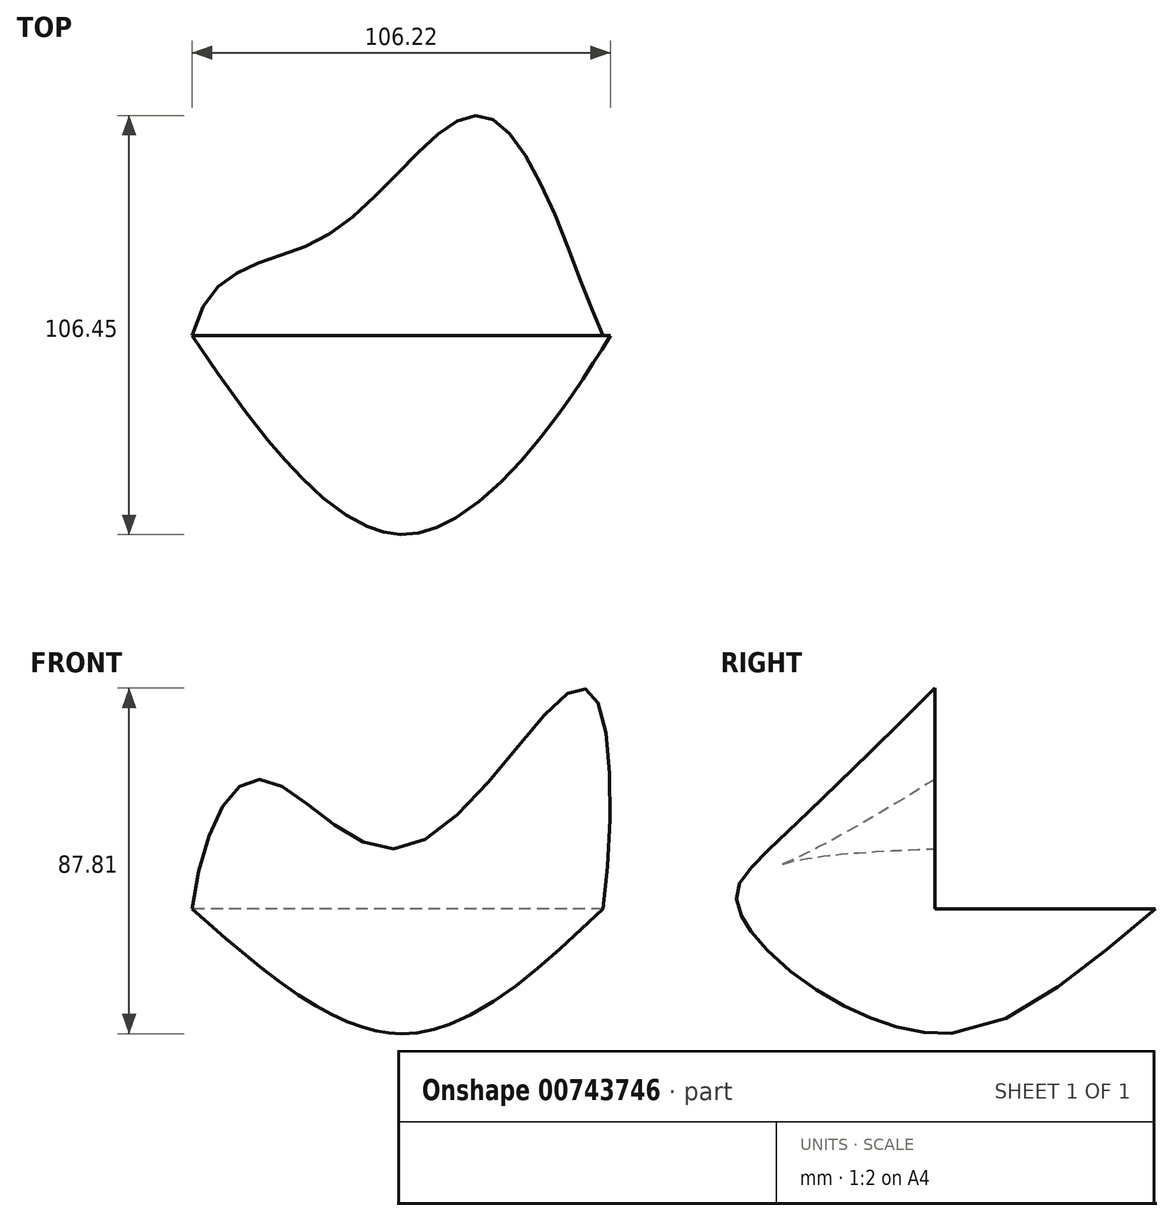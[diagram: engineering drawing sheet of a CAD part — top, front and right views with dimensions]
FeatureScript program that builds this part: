
annotation { "Feature Type Name" : "Feature", "Feature Type Description" : "" }
export const myFeature = defineFeature(function(context is Context, id is Id, definition is map)
    precondition{}
    {
        {
            var Q0;
            Q0=qCreatedBy(makeId("Top.planeOp"),FACE);
            var sketch = newSketch(context, id + "F0", { "sketchPlane" : qUnion([Q0])});
            skFitSpline(sketch, "E0", {"points": [v(-53.72, 0) * mm, v(0, -49.94) * mm, v(50.68, 0) * mm], "startDerivative": vector(107.77, -149.45) * mm, "endDerivative": vector(101.01, 150.21) * mm});
            skSolve(sketch);
        }
        {
            var Q0;
            Q0=qCreatedBy(makeId("Front.planeOp"),FACE);
            var sketch = newSketch(context, id + "F1", { "sketchPlane" : qUnion([Q0])});
            skFitSpline(sketch, "E1", {"points": [v(-53.72, 0) * mm, v(-36.32, 32.96) * mm, v(0, 15.58) * mm, v(45.29, 56.11) * mm, v(50.68, 0) * mm], "startDerivative": vector(26.41, 221.01) * mm, "endDerivative": vector(-30.97, -228.22) * mm});
            skSolve(sketch);
        }
        {
            var Q0;
            Q0=qCreatedBy(makeId("Top.planeOp"),FACE);
            var sketch = newSketch(context, id + "F2", { "sketchPlane" : qUnion([Q0])});
            skPoint(sketch, "E2.0", {"position": v(50.68, 0) * mm});
            skPoint(sketch, "E3.0", {"position": v(-53.72, 0) * mm});
            skFitSpline(sketch, "E4", {"points": [v(50.68, 0) * mm, v(20.59, 55.72) * mm, v(-18.67, 25.93) * mm, v(-53.72, 0) * mm], "startDerivative": vector(-60.39, 130.86) * mm, "endDerivative": vector(-48.83, -200.9) * mm});
            skSolve(sketch);
        }
        {
            var Q0;
            Q0=qCreatedBy(makeId("Front.planeOp"),FACE);
            var sketch = newSketch(context, id + "F3", { "sketchPlane" : qUnion([Q0])});
            skPoint(sketch, "E5.0", {"position": v(-53.72, 0) * mm});
            skPoint(sketch, "E6.0", {"position": v(50.68, 0) * mm});
            skFitSpline(sketch, "E7", {"points": [v(-53.72, 0) * mm, v(0, -31.63) * mm, v(50.68, 0) * mm], "startDerivative": vector(107.29, -94.56) * mm, "endDerivative": vector(101.49, 95.24) * mm});
            skSolve(sketch);
        }
        {
            var Q0;
            Q0=sQuery(id+"F1.wireOp",EDGE,"E1");
            var Q1;
            Q1=sQuery(id+"F0.wireOp",EDGE,"E0");
            var Q2;
            Q2=sQuery(id+"F3.wireOp",EDGE,"E7");
            var Q3;
            Q3=sQuery(id+"F2.wireOp",EDGE,"E4");
            loft(context, id + "F4", {"bodyType" : ToolBodyType.SURFACE, "wireProfilesArray" : [{ "wireProfileEntities" : qUnion([Q0]) }, { "wireProfileEntities" : qUnion([Q1]) }, { "wireProfileEntities" : qUnion([Q2]) }, { "wireProfileEntities" : qUnion([Q3]) }]});
        }
    });
